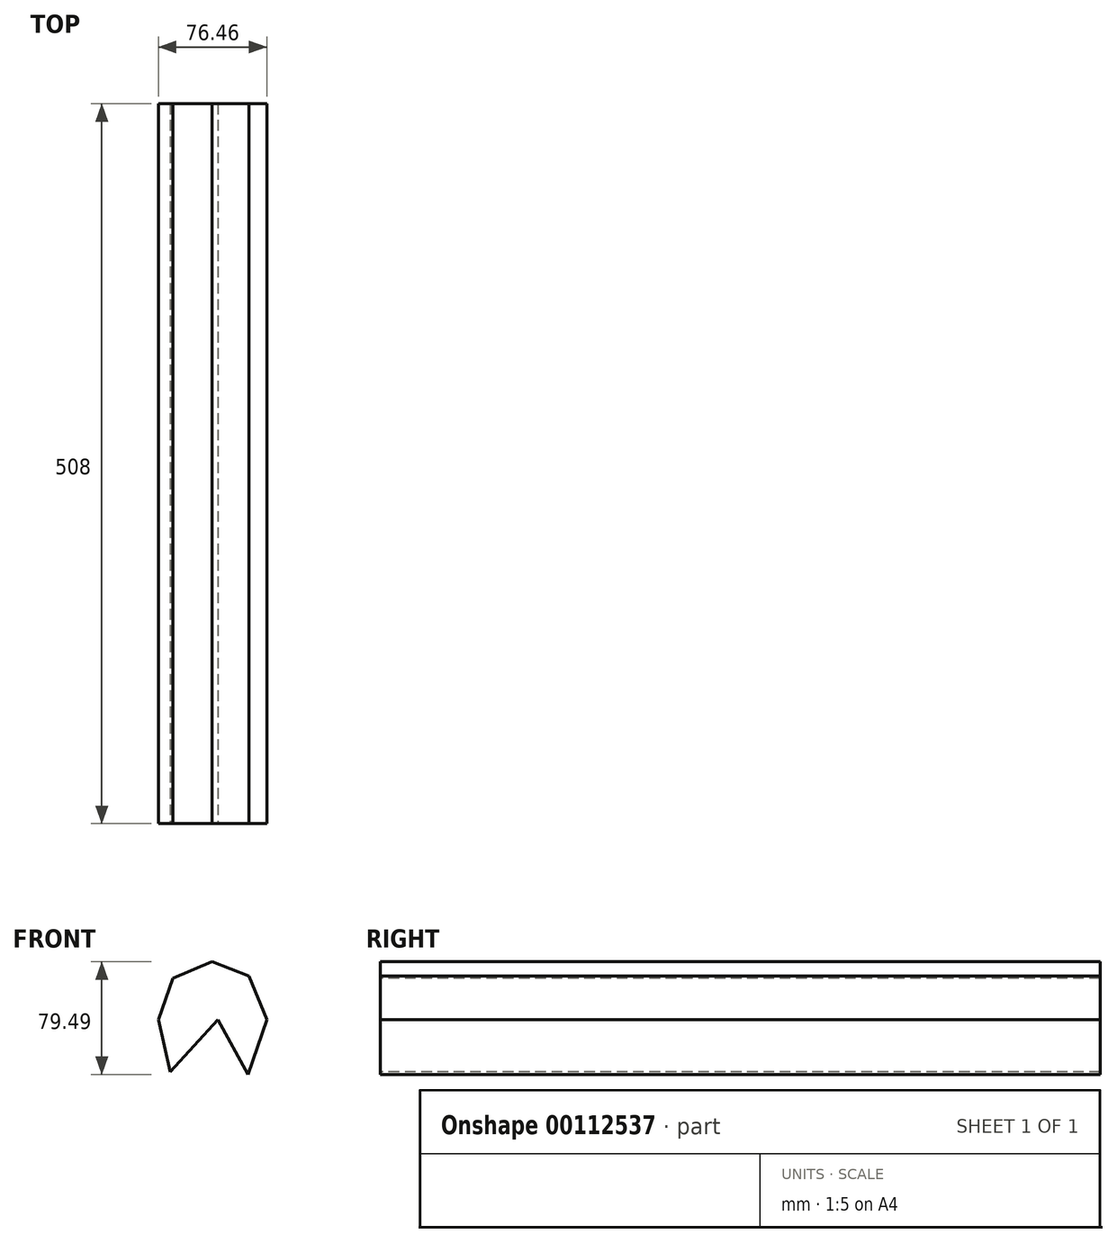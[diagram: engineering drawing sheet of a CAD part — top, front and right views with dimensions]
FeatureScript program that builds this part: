
annotation { "Feature Type Name" : "Feature", "Feature Type Description" : "" }
export const myFeature = defineFeature(function(context is Context, id is Id, definition is map)
    precondition{}
    {
        {
            var Q0;
            Q0=qCreatedBy(makeId("Front.planeOp"),FACE);
            var sketch = newSketch(context, id + "F0", { "sketchPlane" : qUnion([Q0])});
            skArc(sketch, "E0", {"start": v(75.6, 0) * mm, "mid": v(37.8, 40.68) * mm, "end": v(0, 0) * mm});
            skSolve(sketch);
        }
        {
            var Q0;
            Q0=qCreatedBy(makeId("Front.planeOp"),FACE);
            var sketch = newSketch(context, id + "F1", { "sketchPlane" : qUnion([Q0])});
            skLineSegment(sketch, "E1", {"start": v(0, 0) * mm, "end": v(75.6, 0) * mm});
            skSolve(sketch);
        }
        {
            var Q0;
            Q0=sQuery(id+"F0.wireOp",EDGE,"E0");
            extrude(context, id + "F2", {"bodyType" : ToolBodyType.SURFACE, "surfaceEntities" : qUnion([Q0]), "depth" : 254 * mm});
        }
        {
            var Q0;
            Q0=sQuery(id+"F1.wireOp",EDGE,"E1");
            extrude(context, id + "F3", {"bodyType" : ToolBodyType.SURFACE, "surfaceEntities" : qUnion([Q0]), "depth" : 254 * mm});
        }
        {
            var Q0;
            Q0=qCreatedBy(makeId("Front.planeOp"),FACE);
            var sketch = newSketch(context, id + "F4", { "sketchPlane" : qUnion([Q0])});
            skLineSegment(sketch, "E2", {"start": v(0, 0) * mm, "end": v(8.29, -36.75) * mm});
            skLineSegment(sketch, "E3", {"start": v(8.29, -36.75) * mm, "end": v(41.82, 0) * mm});
            skLineSegment(sketch, "E4", {"start": v(41.82, 0) * mm, "end": v(63.13, -38.52) * mm});
            skLineSegment(sketch, "E5", {"start": v(63.13, -38.52) * mm, "end": v(76.46, 0) * mm});
            skLineSegment(sketch, "E6", {"start": v(76.46, 0) * mm, "end": v(63.8, 30.76) * mm});
            skLineSegment(sketch, "E7", {"start": v(63.8, 30.76) * mm, "end": v(37.82, 40.97) * mm});
            skLineSegment(sketch, "E8", {"start": v(37.82, 40.97) * mm, "end": v(10.28, 29.2) * mm});
            skLineSegment(sketch, "E9", {"start": v(10.28, 29.2) * mm, "end": v(0, 0) * mm});
            skSolve(sketch);
        }
        {
            var Q0;
            Q0=makeQuery(id+"F4.imprint","IMPRINT",FACE,{"disambiguationData":[TD([[makeQuery(id+"F4.imprint","IMPRINT",EDGE,{"derivedFrom":sQuery(id+"F4.wireOp",EDGE,"E2")}),1.0]])]});
            extrude(context, id + "F5", {"entities" : qUnion([Q0]), "oppositeDirection" : true, "depth" : 508 * mm});
        }
    });
